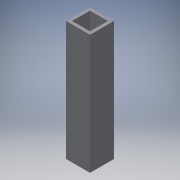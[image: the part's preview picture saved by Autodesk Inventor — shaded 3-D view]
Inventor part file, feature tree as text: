
AUTODESK INVENTOR PART (.ipt)
format: ipt  version: 2016 (Build 200138000, 138)  size: 102,912 bytes
history: native  units: in
note: dims shown in document units (in); Inventor stores cm internally (conversion verified against a paired STEP export)
features: extrude x2, sketch x2
ambient origin geometry x8: Origin, YZ Plane, XZ Plane, XY Plane, X Axis, Y Axis, Z Axis, Center Point
bodies: Solid1 (feature_tree)
feature tree (4):
  extrude  "Extrusion1"  Depth=1.0in
  extrude  "Extrusion2"  Depth=8.0in TaperAngle=0.0deg
  sketch  "Sketch1"  dims[d0=1.0in d1=1.0in]
  sketch  "Sketch2"  dims[d2=0.125in d3=8.0in d4=0.0in d5=0.5in d6=0.5in d7=0.5in d8=1.0in d9=0.0in]
